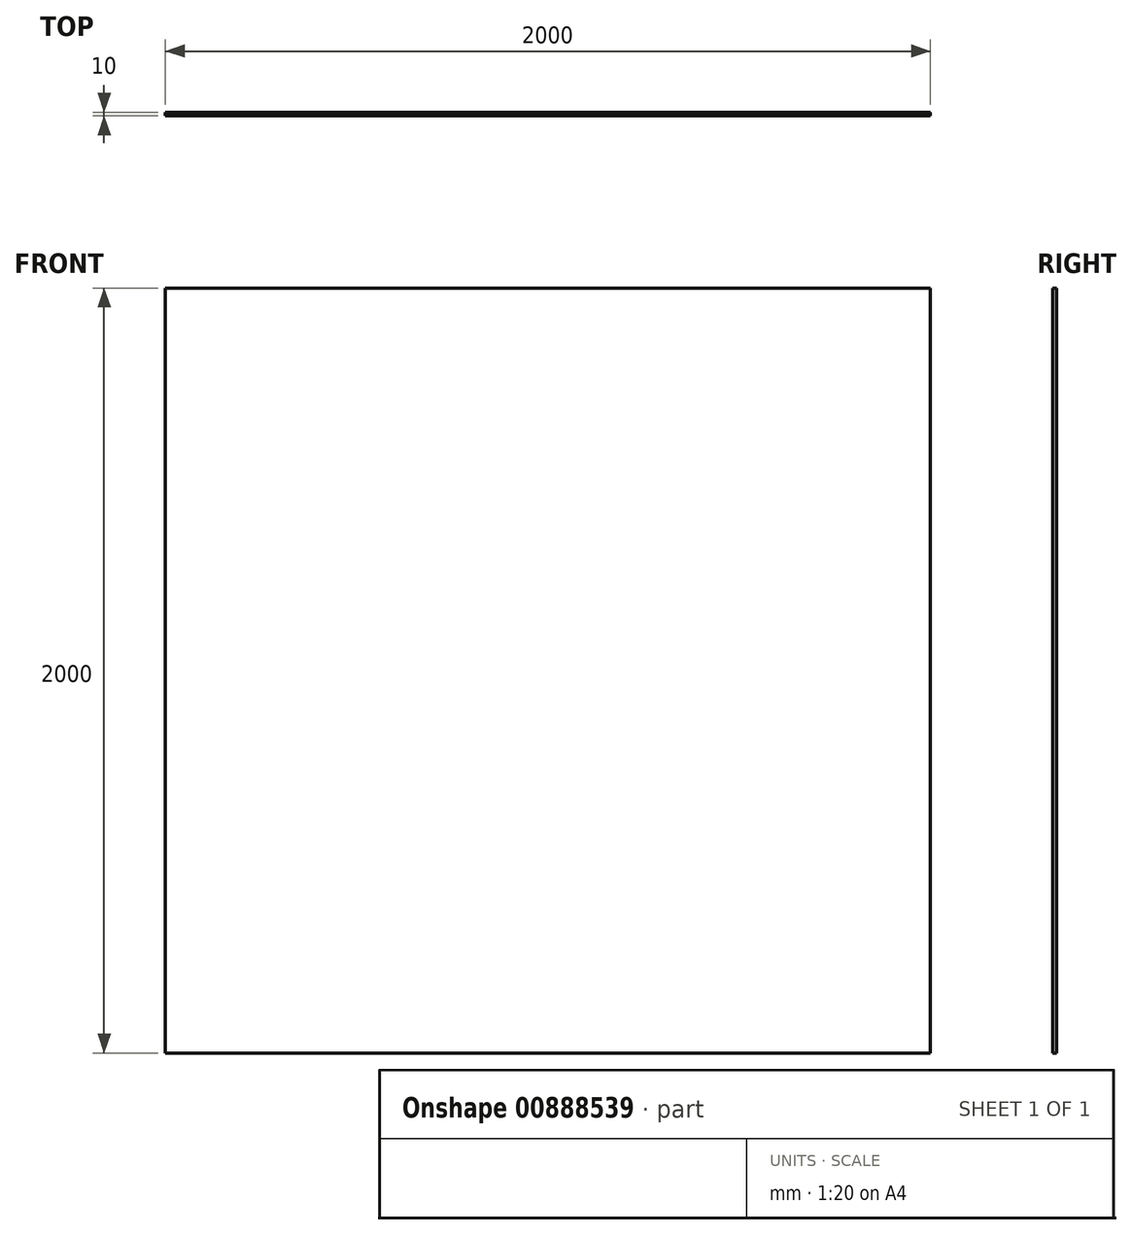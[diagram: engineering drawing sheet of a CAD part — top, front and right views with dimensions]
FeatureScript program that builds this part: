
annotation { "Feature Type Name" : "Feature", "Feature Type Description" : "" }
export const myFeature = defineFeature(function(context is Context, id is Id, definition is map)
    precondition{}
    {
        {
            var Q0;
            Q0=qCreatedBy(makeId("Front.planeOp"),FACE);
            var sketch = newSketch(context, id + "F0", { "sketchPlane" : qUnion([Q0])});
            skLineSegment(sketch, "E0.bottom", {"start": v(-1000, 1000) * mm, "end": v(1000, 1000) * mm});
            skLineSegment(sketch, "E0.top", {"start": v(-1000, -1000) * mm, "end": v(1000, -1000) * mm});
            skLineSegment(sketch, "E0.left", {"start": v(-1000, 1000) * mm, "end": v(-1000, -1000) * mm});
            skLineSegment(sketch, "E0.right", {"start": v(1000, 1000) * mm, "end": v(1000, -1000) * mm});
            skSolve(sketch);
        }
        {
            var Q0;
            Q0 = qSketchRegion(id + "F0", true);
            extrude(context, id + "F1", {"entities" : qUnion([Q0]), "depth" : 10 * mm, "offsetDistance" : 25 * mm});
        }
    });
